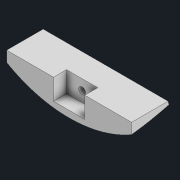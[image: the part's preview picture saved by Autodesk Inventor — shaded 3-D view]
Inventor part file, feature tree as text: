
AUTODESK INVENTOR PART (.ipt)
format: ipt  version: 2022 (Build 260153000, 153)  size: 154,624 bytes
history: native  units: mm
features: sketch x8, extrude x6, projected_geometry x3, revolve x1, hole x1
ambient origin geometry x8: Origin, YZ Plane, XZ Plane, XY Plane, X Axis, Y Axis, Z Axis, Center Point
bodies: Body1 (feature_tree)
feature tree (19):
  revolve  "回転2"
  extrude  "押し出し1"  Depth=120.0mm
  extrude  "押し出し2"  Depth=12.0mm
  extrude  "押し出し3"  Depth=28.0mm
  hole  "穴1"  [1 undecoded]
  extrude  "押し出し4"  Depth=15.0mm
  extrude  "押し出し5"  Depth=20.0mm
  extrude  "押し出し6"  Depth=15.0mm
  sketch  "スケッチ2"
  sketch  "スケッチ3"
  sketch  "スケッチ5"
  projected_geometry  "投影ループ1"
  sketch  "スケッチ7"
  sketch  "スケッチ8"
  sketch  "スケッチ9"
  projected_geometry  "投影ループ2"
  sketch  "スケッチ10"
  projected_geometry  "投影ループ3"
  sketch  "スケッチ11"
note: 1 required parameter value undecoded (feature->parameter linkage not recoverable at this tier; creation-order binding heuristic only, values carry confidence <= 0.55)
